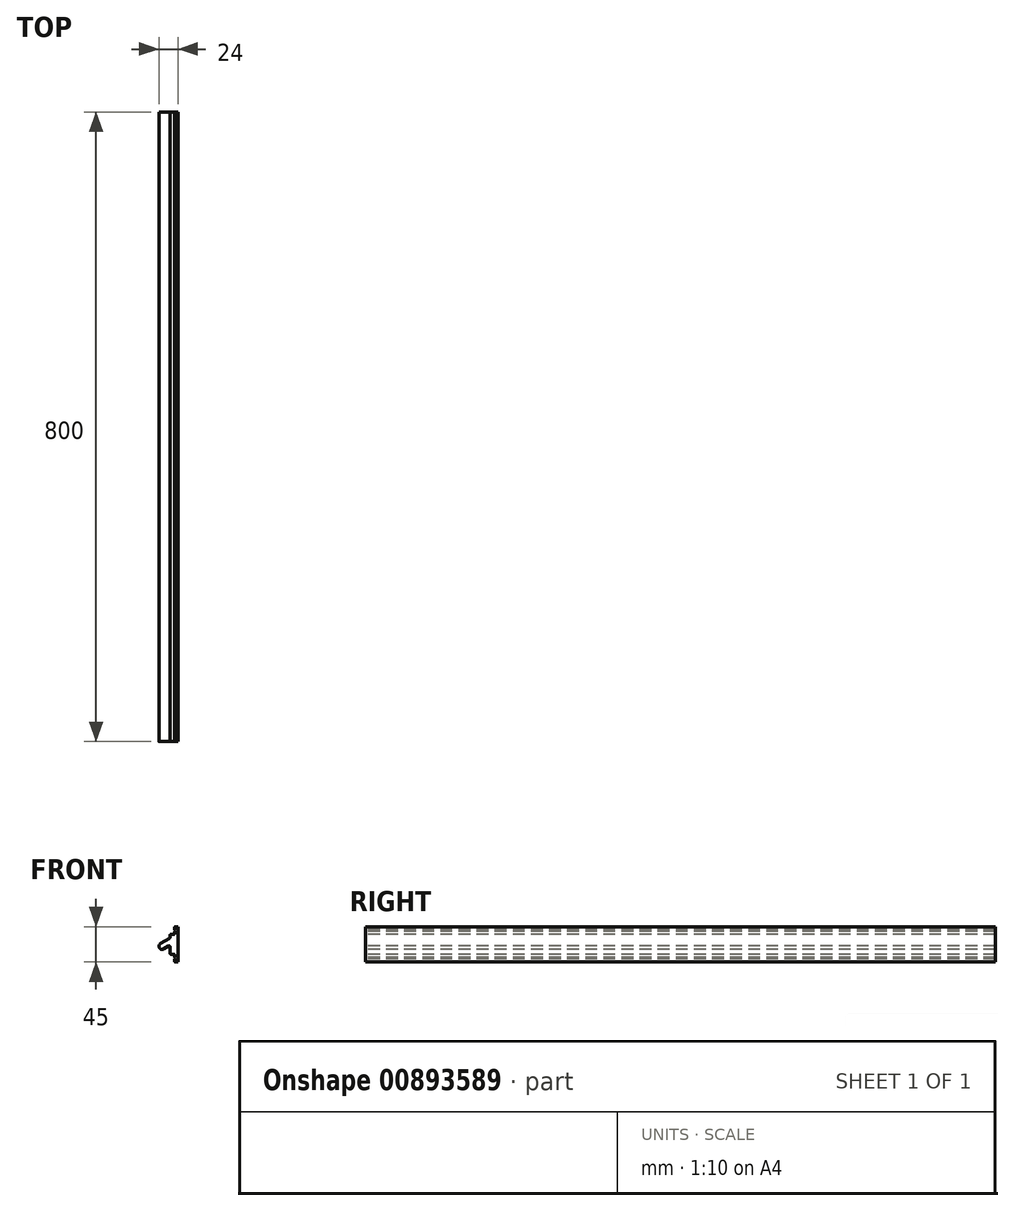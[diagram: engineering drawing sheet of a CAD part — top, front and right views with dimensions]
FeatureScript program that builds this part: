
annotation { "Feature Type Name" : "Feature", "Feature Type Description" : "" }
export const myFeature = defineFeature(function(context is Context, id is Id, definition is map)
    precondition{}
    {
        {
            var Q0;
            Q0=qCreatedBy(makeId("Front.planeOp"),FACE);
            var sketch = newSketch(context, id + "F0", { "sketchPlane" : qUnion([Q0])});
            skLineSegment(sketch, "E0", {"start": v(-10.5, -29.9) * mm, "end": v(-22, -36.54) * mm});
            skArc(sketch, "E1", {"start": v(-22, -36.54) * mm, "mid": v(-23.46, -42) * mm, "end": v(-18, -43.46) * mm});
            skLineSegment(sketch, "E2", {"start": v(-18, -43.46) * mm, "end": v(-11.5, -39.71) * mm});
            skLineSegment(sketch, "E3", {"start": v(-10, -40.58) * mm, "end": v(-10, -49) * mm});
            skArc(sketch, "E4", {"start": v(-10, -49) * mm, "mid": v(-9.7, -49.7) * mm, "end": v(-9, -50) * mm});
            skLineSegment(sketch, "E5", {"start": v(-9, -50) * mm, "end": v(-5, -50) * mm});
            skLineSegment(sketch, "E6", {"start": v(-4, -51) * mm, "end": v(-4, -54) * mm});
            skLineSegment(sketch, "E7", {"start": v(-3, -60) * mm, "end": v(0, -60) * mm});
            skLineSegment(sketch, "E8", {"start": v(0, -60) * mm, "end": v(0, -15) * mm});
            skPoint(sketch, "E9.visualSharp", {"position": v(-10, -38.85) * mm});
            skArc(sketch, "E9.filletArc", {"start": v(-10, -40.58) * mm, "mid": v(-10.5, -39.71) * mm, "end": v(-11.5, -39.71) * mm});
            skPoint(sketch, "E10.visualSharp", {"position": v(-4, -50) * mm});
            skArc(sketch, "E10.filletArc", {"start": v(-4, -51) * mm, "mid": v(-4.3, -50.3) * mm, "end": v(-5, -50) * mm});
            skPoint(sketch, "E11.visualSharp", {"position": v(-4, -60) * mm});
            skArc(sketch, "E11.filletArc", {"start": v(-4, -59) * mm, "mid": v(-3.7, -59.7) * mm, "end": v(-3, -60) * mm});
            skLineSegment(sketch, "E12", {"start": v(0, 0) * mm, "end": v(-9.28, 0) * mm, "construction": true});
            skLineSegment(sketch, "E13", {"start": v(-4, -24) * mm, "end": v(-4, -21) * mm});
            skLineSegment(sketch, "E14", {"start": v(-3, -15) * mm, "end": v(0, -15) * mm});
            skPoint(sketch, "E15.visualSharp", {"position": v(-4, -25) * mm});
            skArc(sketch, "E15.filletArc", {"start": v(-5, -25) * mm, "mid": v(-4.3, -24.7) * mm, "end": v(-4, -24) * mm});
            skPoint(sketch, "E16.visualSharp", {"position": v(-4, -15) * mm});
            skArc(sketch, "E16.filletArc", {"start": v(-3, -15) * mm, "mid": v(-3.7, -15.3) * mm, "end": v(-4, -16) * mm});
            skLineSegment(sketch, "E17", {"start": v(-4, -19) * mm, "end": v(-3, -20) * mm});
            skLineSegment(sketch, "E18", {"start": v(-3, -20) * mm, "end": v(-4, -21) * mm});
            skLineSegment(sketch, "E19.trimOffspring", {"start": v(-4, -19) * mm, "end": v(-4, -16) * mm});
            skLineSegment(sketch, "E20", {"start": v(-4, -54) * mm, "end": v(-3, -55) * mm});
            skLineSegment(sketch, "E21", {"start": v(-3, -55) * mm, "end": v(-4, -56) * mm});
            skLineSegment(sketch, "E22.trimOffspring", {"start": v(-4, -56) * mm, "end": v(-4, -59) * mm});
            skLineSegment(sketch, "E23", {"start": v(-10, -29.03) * mm, "end": v(-10, -26) * mm});
            skLineSegment(sketch, "E24", {"start": v(-5, -25) * mm, "end": v(-9, -25) * mm});
            skPoint(sketch, "E25.visualSharp", {"position": v(-10, -29.6) * mm});
            skArc(sketch, "E25.filletArc", {"start": v(-10.5, -29.9) * mm, "mid": v(-10.13, -29.53) * mm, "end": v(-10, -29.03) * mm});
            skPoint(sketch, "E26.visualSharp", {"position": v(-10, -25) * mm});
            skArc(sketch, "E26.filletArc", {"start": v(-9, -25) * mm, "mid": v(-9.7, -25.3) * mm, "end": v(-10, -26) * mm});
            skSolve(sketch);
        }
        {
            var Q0;
            Q0=qSketchRegion(id+"F0",true);
            extrude(context, id + "F1", {"entities" : qUnion([Q0]), "oppositeDirection" : true, "depth" : 800 * mm, "offsetDistance" : 25 * mm});
        }
    });
